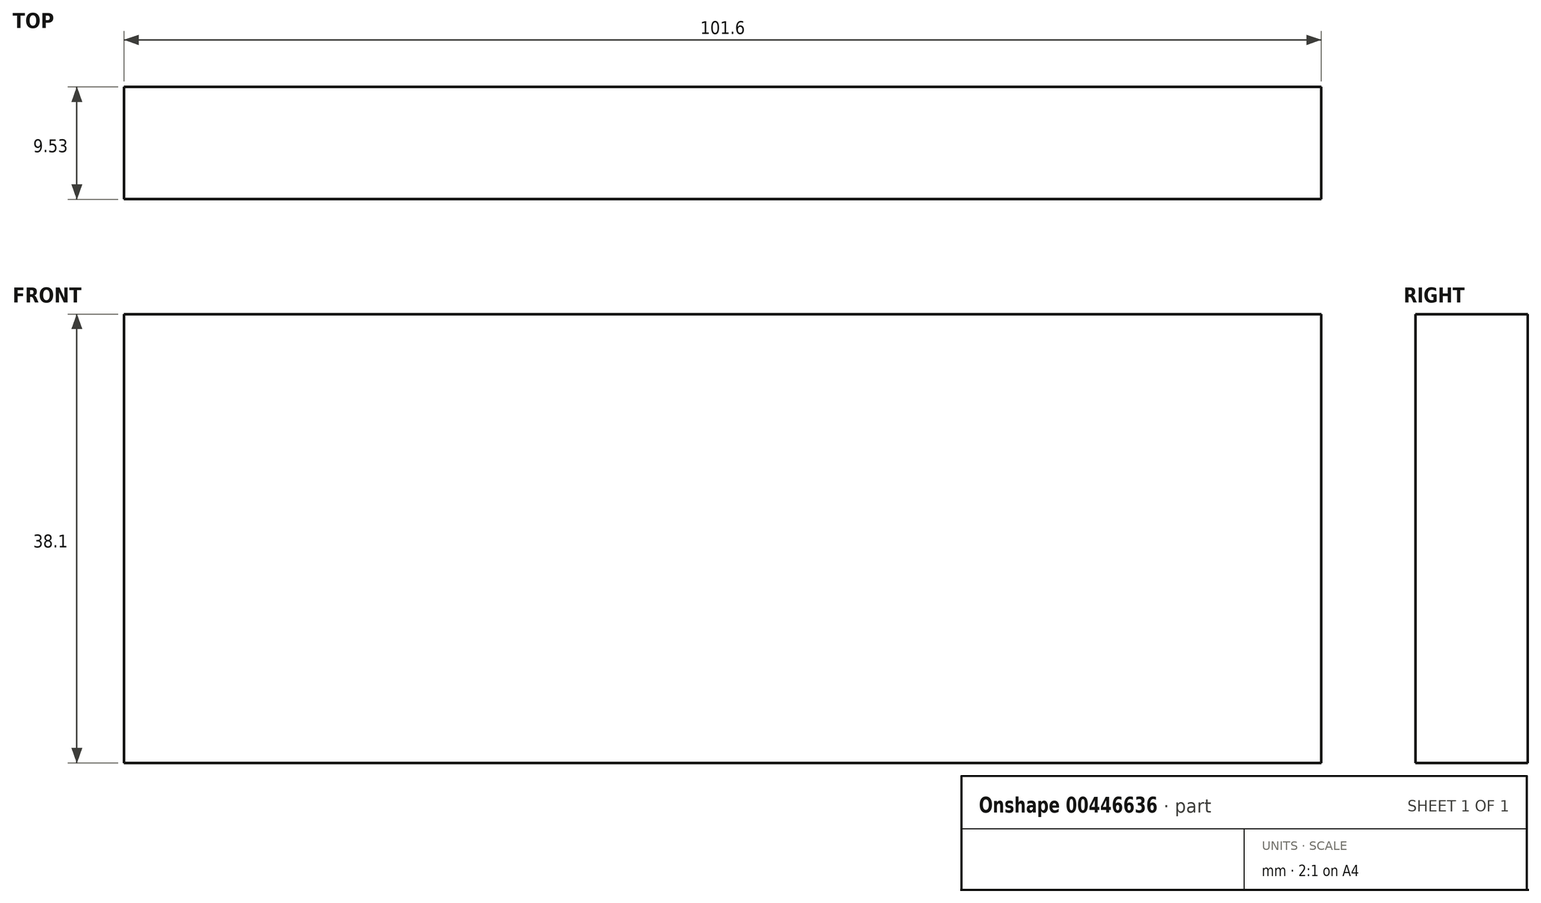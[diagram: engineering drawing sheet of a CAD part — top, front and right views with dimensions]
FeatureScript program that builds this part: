
annotation { "Feature Type Name" : "Feature", "Feature Type Description" : "" }
export const myFeature = defineFeature(function(context is Context, id is Id, definition is map)
    precondition{}
    {
        {
            var Q0;
            Q0=qCreatedBy(makeId("Front.planeOp"),FACE);
            var sketch = newSketch(context, id + "F0", { "sketchPlane" : qUnion([Q0])});
            skLineSegment(sketch, "E0.bottom", {"start": v(0, 0) * mm, "end": v(101.6, 0) * mm});
            skLineSegment(sketch, "E0.top", {"start": v(0, -38.1) * mm, "end": v(101.6, -38.1) * mm});
            skLineSegment(sketch, "E0.left", {"start": v(0, 0) * mm, "end": v(0, -38.1) * mm});
            skLineSegment(sketch, "E0.right", {"start": v(101.6, 0) * mm, "end": v(101.6, -38.1) * mm});
            skSolve(sketch);
        }
        {
            var Q0;
            Q0 = qSketchRegion(id + "F0", true);
            extrude(context, id + "F1", {"entities" : qUnion([Q0]), "depth" : 9.52 * mm});
        }
    });
